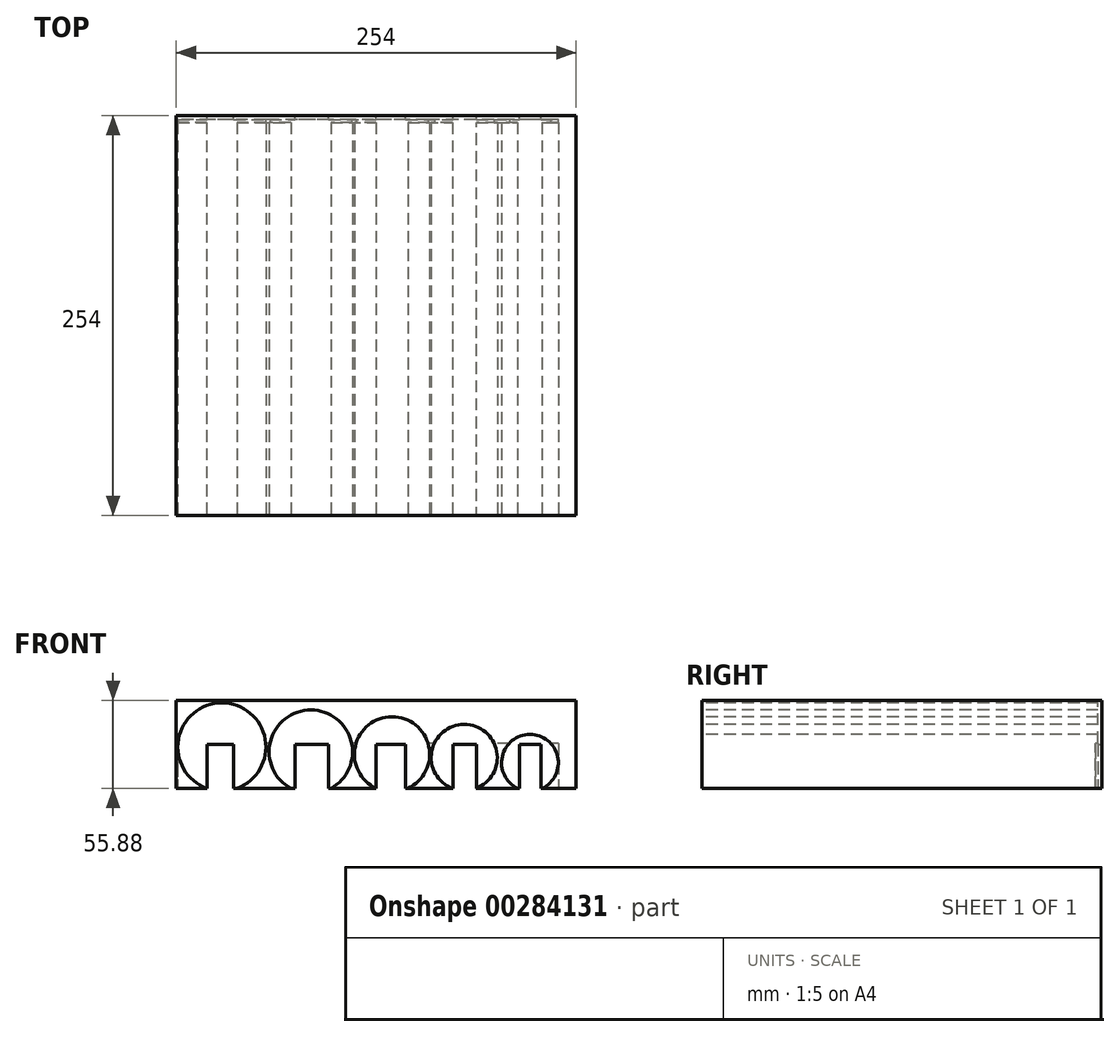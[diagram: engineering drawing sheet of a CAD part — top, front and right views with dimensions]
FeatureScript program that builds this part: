
annotation { "Feature Type Name" : "Feature", "Feature Type Description" : "" }
export const myFeature = defineFeature(function(context is Context, id is Id, definition is map)
    precondition{}
    {
        {
            var Q0;
            Q0=qCreatedBy(makeId("Front.planeOp"),FACE);
            var sketch = newSketch(context, id + "F0", { "sketchPlane" : qUnion([Q0])});
            skLineSegment(sketch, "E0.bottom", {"start": v(-127, 27.94) * mm, "end": v(127, 27.94) * mm});
            skLineSegment(sketch, "E0.top", {"start": v(-127, -27.94) * mm, "end": v(127, -27.94) * mm});
            skLineSegment(sketch, "E0.left", {"start": v(-127, 27.94) * mm, "end": v(-127, -27.94) * mm});
            skLineSegment(sketch, "E0.right", {"start": v(127, 27.94) * mm, "end": v(127, -27.94) * mm});
            skPoint(sketch, "E0.middle", {"position": v(0, 0) * mm});
            skSolve(sketch);
        }
        {
            var Q0;
            Q0=makeQuery(id+"F0.imprint","IMPRINT",FACE,{"disambiguationData":[TD([[makeQuery(id+"F0.imprint","IMPRINT",EDGE,{"derivedFrom":sQuery(id+"F0.wireOp",EDGE,"E0.bottom")}),-1.0]])]});
            extrude(context, id + "F1", {"entities" : qUnion([Q0]), "depth" : 254 * mm});
        }
        {
            var Q0;
            Q0=makeQuery(id+"F1.opExtrude","CAP_FACE",FACE,{"disambiguationData":[OSD([sQuery(id+"F0.wireOp",EDGE,"E0.bottom"),sQuery(id+"F0.wireOp",EDGE,"E0.top"),sQuery(id+"F0.wireOp",EDGE,"E0.left"),sQuery(id+"F0.wireOp",EDGE,"E0.right")])],"isStart":false});
            var sketch = newSketch(context, id + "F2", { "sketchPlane" : qUnion([Q0])});
            skArc(sketch, "E1", {"start": v(-88.41, -27.94) * mm, "mid": v(-98, 26.37) * mm, "end": v(-107.6, -27.94) * mm});
            skLineSegment(sketch, "E2.0", {"start": v(-127, -27.94) * mm, "end": v(127, -27.94) * mm});
            skSolve(sketch);
        }
        {
            var Q0;
            {var subQ2=sQuery(id+"F2.wireOp",EDGE,"E1");Q0=makeQuery(id+"F2.imprint","IMPRINT",FACE,{"disambiguationData":[TD([[makeQuery(id+"F2.imprint","IMPRINT",EDGE,{"derivedFrom":subQ2}),-1.0]])]});}
            var sketch = newSketch(context, id + "F3", { "sketchPlane" : qUnion([Q0])});
            skLineSegment(sketch, "E3.0", {"start": v(-127, -27.94) * mm, "end": v(127, -27.94) * mm});
            skArc(sketch, "E4", {"start": v(-28.8, -27.94) * mm, "mid": v(-41.48, 21.83) * mm, "end": v(-54.17, -27.94) * mm});
            skSolve(sketch);
        }
        {
            var Q0;
            {var subQ2=sQuery(id+"F2.wireOp",EDGE,"E1");Q0=makeQuery(id+"F2.imprint","IMPRINT",FACE,{"disambiguationData":[TD([[makeQuery(id+"F2.imprint","IMPRINT",EDGE,{"derivedFrom":subQ2}),-1.0]])]});}
            var sketch = newSketch(context, id + "F4", { "sketchPlane" : qUnion([Q0])});
            skLineSegment(sketch, "E5.0", {"start": v(-127, -27.94) * mm, "end": v(127, -27.94) * mm});
            skArc(sketch, "E6", {"start": v(20.14, -27.94) * mm, "mid": v(10.07, 17.6) * mm, "end": v(0, -27.94) * mm});
            skSolve(sketch);
        }
        {
            var Q0;
            {var subQ2=sQuery(id+"F2.wireOp",EDGE,"E1");Q0=makeQuery(id+"F2.imprint","IMPRINT",FACE,{"disambiguationData":[TD([[makeQuery(id+"F2.imprint","IMPRINT",EDGE,{"derivedFrom":subQ2}),-1.0]])]});}
            var sketch = newSketch(context, id + "F5", { "sketchPlane" : qUnion([Q0])});
            skLineSegment(sketch, "E7.0", {"start": v(-127, -27.94) * mm, "end": v(127, -27.94) * mm});
            skArc(sketch, "E8", {"start": v(63.36, -27.94) * mm, "mid": v(55.92, 12.7) * mm, "end": v(48.5, -27.94) * mm});
            skSolve(sketch);
        }
        {
            var Q0;
            {var subQ2=sQuery(id+"F2.wireOp",EDGE,"E1");Q0=makeQuery(id+"F2.imprint","IMPRINT",FACE,{"disambiguationData":[TD([[makeQuery(id+"F2.imprint","IMPRINT",EDGE,{"derivedFrom":subQ2}),-1.0]])]});}
            var sketch = newSketch(context, id + "F6", { "sketchPlane" : qUnion([Q0])});
            skLineSegment(sketch, "E9.0", {"start": v(-127, -27.94) * mm, "end": v(127, -27.94) * mm});
            skArc(sketch, "E10", {"start": v(105.44, -27.94) * mm, "mid": v(97.67, 6.36) * mm, "end": v(89.9, -27.94) * mm});
            skSolve(sketch);
        }
        {
            var Q0;
            {var subQ0=sQuery(id+"F6.wireOp",EDGE,"E10");Q0=makeQuery(id+"F6.imprint","IMPRINT",FACE,{"disambiguationData":[TD([[makeQuery(id+"F6.imprint","IMPRINT",EDGE,{"derivedFrom":subQ0}),1.0]])]});}
            extrude(context, id + "F7", {"entities" : qUnion([Q0]), "operationType" : NewBodyOperationType.REMOVE, "oppositeDirection" : true, "depth" : 251.46 * mm});
        }
        {
            var Q0;
            {var subQ0=sQuery(id+"F5.wireOp",EDGE,"E8");Q0=makeQuery(id+"F5.imprint","IMPRINT",FACE,{"disambiguationData":[TD([[makeQuery(id+"F5.imprint","IMPRINT",EDGE,{"derivedFrom":subQ0}),1.0]])]});}
            extrude(context, id + "F8", {"entities" : qUnion([Q0]), "operationType" : NewBodyOperationType.REMOVE, "oppositeDirection" : true, "depth" : 251.46 * mm});
        }
        {
            var Q0;
            {var subQ0=sQuery(id+"F4.wireOp",EDGE,"E6");Q0=makeQuery(id+"F4.imprint","IMPRINT",FACE,{"disambiguationData":[TD([[makeQuery(id+"F4.imprint","IMPRINT",EDGE,{"derivedFrom":subQ0}),1.0]])]});}
            extrude(context, id + "F9", {"entities" : qUnion([Q0]), "operationType" : NewBodyOperationType.REMOVE, "oppositeDirection" : true, "depth" : 251.46 * mm});
        }
        {
            var Q0;
            {var subQ0=sQuery(id+"F3.wireOp",EDGE,"E4");Q0=makeQuery(id+"F3.imprint","IMPRINT",FACE,{"disambiguationData":[TD([[makeQuery(id+"F3.imprint","IMPRINT",EDGE,{"derivedFrom":subQ0}),1.0]])]});}
            extrude(context, id + "F10", {"entities" : qUnion([Q0]), "operationType" : NewBodyOperationType.REMOVE, "oppositeDirection" : true, "depth" : 251.46 * mm});
        }
        {
            var Q0;
            {var subQ0=sQuery(id+"F2.wireOp",EDGE,"E1");Q0=makeQuery(id+"F2.imprint","IMPRINT",FACE,{"disambiguationData":[TD([[makeQuery(id+"F2.imprint","IMPRINT",EDGE,{"derivedFrom":subQ0}),1.0]])]});}
            extrude(context, id + "F11", {"entities" : qUnion([Q0]), "operationType" : NewBodyOperationType.REMOVE, "oppositeDirection" : true, "depth" : 251.46 * mm});
        }
        {
            var Q0;
            Q0=makeQuery(id+"F1.opExtrude","SWEPT_FACE",FACE,{"disambiguationData":[OSD([sQuery(id+"F0.wireOp",EDGE,"E0.top")])]});
            var sketch = newSketch(context, id + "F12", { "sketchPlane" : qUnion([Q0])});
            skLineSegment(sketch, "E11.0.0", {"start": v(-126, 254) * mm, "end": v(-70, 254) * mm});
            skLineSegment(sketch, "E11.0.1", {"start": v(-107.6, 254) * mm, "end": v(-107.6, 2.54) * mm});
            skLineSegment(sketch, "E11.0.2", {"start": v(-70, 2.54) * mm, "end": v(-126, 2.54) * mm});
            skLineSegment(sketch, "E11.0.3", {"start": v(-88.41, 2.54) * mm, "end": v(-88.41, 254) * mm});
            skLineSegment(sketch, "E12", {"start": v(-126, 4.34) * mm, "end": v(-70, 4.34) * mm});
            skLineSegment(sketch, "E13", {"start": v(-126, 2.54) * mm, "end": v(-126, 4.34) * mm});
            skLineSegment(sketch, "E14.0.0", {"start": v(79.64, 254) * mm, "end": v(115.7, 254) * mm});
            skLineSegment(sketch, "E14.0.1", {"start": v(89.9, 254) * mm, "end": v(89.9, 2.54) * mm});
            skLineSegment(sketch, "E14.0.2", {"start": v(115.7, 2.54) * mm, "end": v(79.64, 2.54) * mm});
            skLineSegment(sketch, "E14.0.3", {"start": v(105.44, 2.54) * mm, "end": v(105.44, 254) * mm});
            skLineSegment(sketch, "E15", {"start": v(-70, 4.34) * mm, "end": v(115.7, 4.34) * mm});
            skLineSegment(sketch, "E16", {"start": v(115.7, 4.34) * mm, "end": v(115.7, 2.54) * mm});
            skLineSegment(sketch, "E17", {"start": v(-70, 2.54) * mm, "end": v(79.64, 2.54) * mm});
            skSolve(sketch);
        }
        {
            var Q0;
            {var subQ5=sQuery(id+"F12.wireOp",EDGE,"E13");Q0=makeQuery(id+"F12.imprint","IMPRINT",FACE,{"disambiguationData":[TD([[makeQuery(id+"F12.imprint","IMPRINT",EDGE,{"derivedFrom":subQ5}),-1.0]])]});}
            var Q1;
            {var subQ7=sQuery(id+"F12.wireOp",EDGE,"E11.0.3");var subQ9=sQuery(id+"F12.wireOp",EDGE,"E17");var subQ11=sQuery(id+"F12.wireOp",EDGE,"E11.0.2");var subQ12=makeQuery(id+"F12.imprint","INTERSECT",VERTEX,{"derivedFrom":[subQ11,subQ9]});var subQ13=makeQuery(id+"F12.imprint","INTERSECT",VERTEX,{"derivedFrom":[subQ11,subQ7]});Q1=makeQuery(id+"F12.imprint","IMPRINT",FACE,{"disambiguationData":[TD([[makeQuery(id+"F12.imprint","IMPRINT",EDGE,{"disambiguationData":[TD([[subQ13,1.0],[subQ12,-1.0]])],"derivedFrom":subQ11}),-1.0]])]});}
            var Q2;
            {var subQ0=sQuery(id+"F12.wireOp",EDGE,"E15");var subQ1=sQuery(id+"F3.wireOp",EDGE,"E4");var subQ2=sQuery(id+"F3.wireOp",EDGE,"E3.0");var subQ3=makeQuery(id+"F10.boolean.opBoolean","COPY",EDGE,{"derivedFrom":makeQuery(id+"F10.opExtrude","SWEPT_EDGE",EDGE,{"disambiguationData":[OSD([subQ2,subQ1]),TDD([makeQuery(id+"F3.imprint","INTERSECT",VERTEX,{"disambiguationData":[OD(0.0)],"derivedFrom":[subQ2,subQ1]})])]})});var subQ4=makeQuery(id+"F12.imprint","INTERSECT",VERTEX,{"derivedFrom":[subQ3,subQ0]});Q2=makeQuery(id+"F12.imprint","IMPRINT",FACE,{"disambiguationData":[TD([[makeQuery(id+"F12.imprint","IMPRINT",EDGE,{"disambiguationData":[TD([[subQ4,-1.0]])],"derivedFrom":subQ0}),-1.0]])]});}
            var Q3;
            {var subQ0=sQuery(id+"F12.wireOp",EDGE,"E15");var subQ1=sQuery(id+"F4.wireOp",EDGE,"E6");var subQ2=sQuery(id+"F4.wireOp",EDGE,"E5.0");var subQ3=makeQuery(id+"F9.boolean.opBoolean","COPY",EDGE,{"derivedFrom":makeQuery(id+"F9.opExtrude","SWEPT_EDGE",EDGE,{"disambiguationData":[OSD([subQ2,subQ1]),TDD([makeQuery(id+"F4.imprint","INTERSECT",VERTEX,{"disambiguationData":[OD(0.0)],"derivedFrom":[subQ2,subQ1]})])]})});var subQ4=makeQuery(id+"F12.imprint","INTERSECT",VERTEX,{"derivedFrom":[subQ3,subQ0]});Q3=makeQuery(id+"F12.imprint","IMPRINT",FACE,{"disambiguationData":[TD([[makeQuery(id+"F12.imprint","IMPRINT",EDGE,{"disambiguationData":[TD([[subQ4,-1.0]])],"derivedFrom":subQ0}),-1.0]])]});}
            var Q4;
            {var subQ5=sQuery(id+"F12.wireOp",EDGE,"E14.0.2");var subQ8=sQuery(id+"F12.wireOp",EDGE,"E14.0.1");var subQ11=makeQuery(id+"F12.imprint","INTERSECT",VERTEX,{"derivedFrom":[subQ8,subQ5]});Q4=makeQuery(id+"F12.imprint","IMPRINT",FACE,{"disambiguationData":[TD([[makeQuery(id+"F12.imprint","IMPRINT",EDGE,{"disambiguationData":[TD([[subQ11,-1.0]])],"derivedFrom":subQ8}),1.0]])]});}
            var Q5;
            {var subQ3=sQuery(id+"F12.wireOp",EDGE,"E16");Q5=makeQuery(id+"F12.imprint","IMPRINT",FACE,{"disambiguationData":[TD([[makeQuery(id+"F12.imprint","IMPRINT",EDGE,{"derivedFrom":subQ3}),-1.0]])]});}
            extrude(context, id + "F13", {"entities" : qUnion([Q0, Q1, Q2, Q3, Q4, Q5]), "operationType" : NewBodyOperationType.REMOVE, "oppositeDirection" : true, "depth" : 28.7 * mm});
        }
        {
            var Q0;
            Q0=makeQuery(id+"F1.opExtrude","CAP_FACE",FACE,{"disambiguationData":[OSD([sQuery(id+"F0.wireOp",EDGE,"E0.bottom"),sQuery(id+"F0.wireOp",EDGE,"E0.top"),sQuery(id+"F0.wireOp",EDGE,"E0.left"),sQuery(id+"F0.wireOp",EDGE,"E0.right")])],"isStart":true});
            var sketch = newSketch(context, id + "F14", { "sketchPlane" : qUnion([Q0])});
            skLineSegment(sketch, "E18", {"start": v(107.5, -27.94) * mm, "end": v(107.5, 0) * mm});
            skLineSegment(sketch, "E19", {"start": v(107.5, 0) * mm, "end": v(90.55, 0) * mm});
            skLineSegment(sketch, "E20", {"start": v(90.55, 0) * mm, "end": v(90.55, -27.94) * mm});
            skLineSegment(sketch, "E21", {"start": v(90.55, -27.94) * mm, "end": v(107.5, -27.94) * mm});
            skLineSegment(sketch, "E22", {"start": v(51.66, -27.94) * mm, "end": v(51.66, 0) * mm});
            skLineSegment(sketch, "E23", {"start": v(51.66, 0) * mm, "end": v(30.15, 0) * mm});
            skLineSegment(sketch, "E24", {"start": v(30.15, 0) * mm, "end": v(30.15, -27.94) * mm});
            skLineSegment(sketch, "E25", {"start": v(30.15, -27.94) * mm, "end": v(51.66, -27.94) * mm});
            skLineSegment(sketch, "E26", {"start": v(0, -27.94) * mm, "end": v(0, 0) * mm});
            skLineSegment(sketch, "E27", {"start": v(0, 0) * mm, "end": v(-18.74, 0) * mm});
            skLineSegment(sketch, "E28", {"start": v(-18.74, 0) * mm, "end": v(-18.74, -27.94) * mm});
            skLineSegment(sketch, "E29", {"start": v(-18.74, -27.94) * mm, "end": v(0, -27.94) * mm});
            skLineSegment(sketch, "E30", {"start": v(-48.84, -27.94) * mm, "end": v(-48.84, 0) * mm});
            skLineSegment(sketch, "E31", {"start": v(-48.84, 0) * mm, "end": v(-63.66, 0) * mm});
            skLineSegment(sketch, "E32", {"start": v(-63.66, 0) * mm, "end": v(-63.66, -27.94) * mm});
            skLineSegment(sketch, "E33", {"start": v(-63.66, -27.94) * mm, "end": v(-48.84, -27.94) * mm});
            skLineSegment(sketch, "E34", {"start": v(-91.1, -27.94) * mm, "end": v(-91.1, 0) * mm});
            skLineSegment(sketch, "E35", {"start": v(-91.1, 0) * mm, "end": v(-104.6, 0) * mm});
            skLineSegment(sketch, "E36", {"start": v(-104.6, 0) * mm, "end": v(-104.6, -27.94) * mm});
            skLineSegment(sketch, "E37", {"start": v(-104.6, -27.94) * mm, "end": v(-91.1, -27.94) * mm});
            skSolve(sketch);
        }
        {
            var Q0;
            Q0=makeQuery(id+"F14.imprint","IMPRINT",FACE,{"disambiguationData":[TD([[makeQuery(id+"F14.imprint","IMPRINT",EDGE,{"derivedFrom":sQuery(id+"F14.wireOp",EDGE,"E34")}),1.0]])]});
            var Q1;
            Q1=makeQuery(id+"F14.imprint","IMPRINT",FACE,{"disambiguationData":[TD([[makeQuery(id+"F14.imprint","IMPRINT",EDGE,{"derivedFrom":sQuery(id+"F14.wireOp",EDGE,"E30")}),1.0]])]});
            var Q2;
            Q2=makeQuery(id+"F14.imprint","IMPRINT",FACE,{"disambiguationData":[TD([[makeQuery(id+"F14.imprint","IMPRINT",EDGE,{"derivedFrom":sQuery(id+"F14.wireOp",EDGE,"E26")}),1.0]])]});
            var Q3;
            Q3=makeQuery(id+"F14.imprint","IMPRINT",FACE,{"disambiguationData":[TD([[makeQuery(id+"F14.imprint","IMPRINT",EDGE,{"derivedFrom":sQuery(id+"F14.wireOp",EDGE,"E22")}),1.0]])]});
            var Q4;
            Q4=makeQuery(id+"F14.imprint","IMPRINT",FACE,{"disambiguationData":[TD([[makeQuery(id+"F14.imprint","IMPRINT",EDGE,{"derivedFrom":sQuery(id+"F14.wireOp",EDGE,"E18")}),1.0]])]});
            extrude(context, id + "F15", {"entities" : qUnion([Q0, Q1, Q2, Q3, Q4]), "operationType" : NewBodyOperationType.REMOVE, "oppositeDirection" : true, "depth" : 76.2 * mm});
        }
    });
